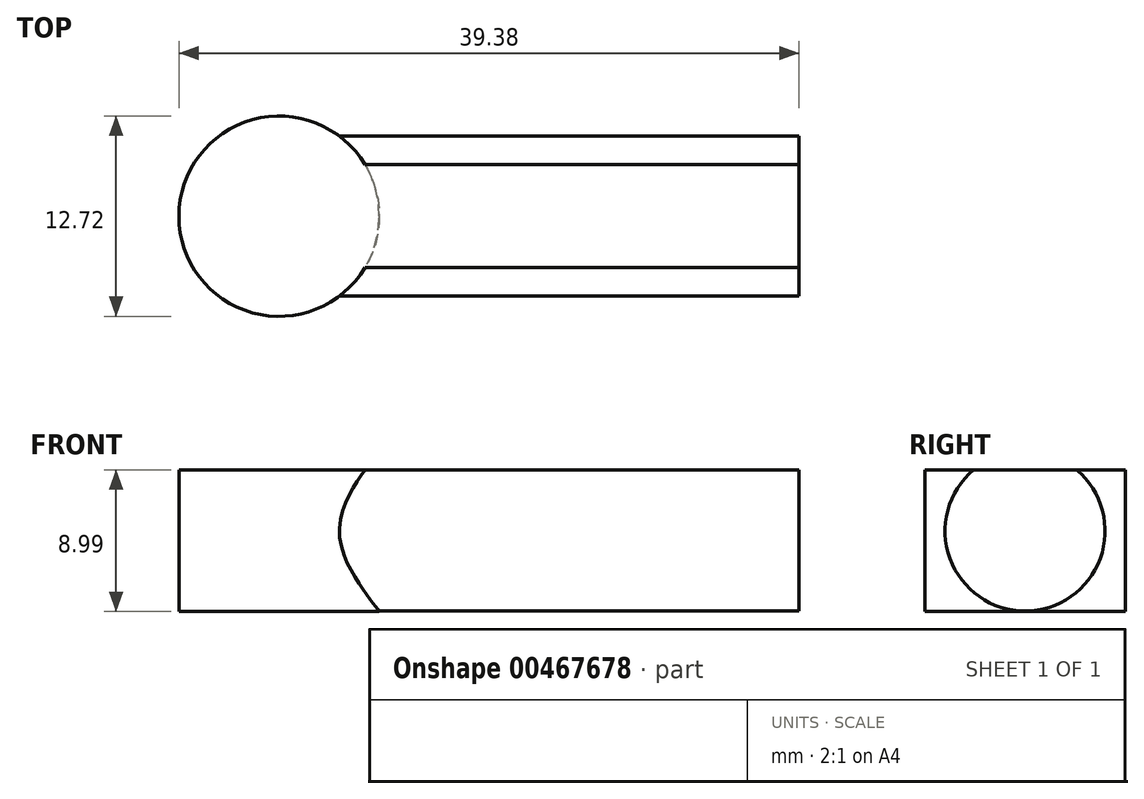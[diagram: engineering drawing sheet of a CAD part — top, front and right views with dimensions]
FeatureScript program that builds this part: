
annotation { "Feature Type Name" : "Feature", "Feature Type Description" : "" }
export const myFeature = defineFeature(function(context is Context, id is Id, definition is map)
    precondition{}
    {
        {
            var Q0;
            Q0=qCreatedBy(makeId("Top.planeOp"),FACE);
            var sketch = newSketch(context, id + "F0", { "sketchPlane" : qUnion([Q0])});
            skCircle(sketch, "E0", {"center": v(0, 0) * mm, "radius": 6.36 * mm});
            skSolve(sketch);
        }
        {
            var Q0;
            Q0=makeQuery(id+"F0.imprint","IMPRINT",FACE,{"disambiguationData":[TD([[makeQuery(id+"F0.imprint","IMPRINT",EDGE,{"derivedFrom":sQuery(id+"F0.wireOp",EDGE,"E0")}),1.0]])]});
            extrude(context, id + "F1", {"entities" : qUnion([Q0]), "oppositeDirection" : true, "depth" : 9 * mm});
        }
        {
            var Q0;
            Q0=qCreatedBy(makeId("Right.planeOp"),FACE);
            var sketch = newSketch(context, id + "F2", { "sketchPlane" : qUnion([Q0])});
            skCircle(sketch, "E1", {"center": v(0, -3.89) * mm, "radius": 5.08 * mm});
            skSolve(sketch);
        }
        {
            var Q0;
            Q0 = qSketchRegion(id + "F2", true);
            extrude(context, id + "F3", {"entities" : qUnion([Q0]), "operationType" : NewBodyOperationType.ADD, "depth" : 33.02 * mm});
        }
        {
            var Q0;
            Q0=makeQuery(id+"F3.opExtrude","CAP_FACE",FACE,{"disambiguationData":[OSD([sQuery(id+"F2.wireOp",EDGE,"E1")])],"isStart":true});
            extrude(context, id + "F4", {"entities" : qUnion([Q0]), "operationType" : NewBodyOperationType.REMOVE, "endBound" : BoundingType.UP_TO_NEXT, "oppositeDirection" : true, "depth" : 25.4 * mm});
        }
    });
